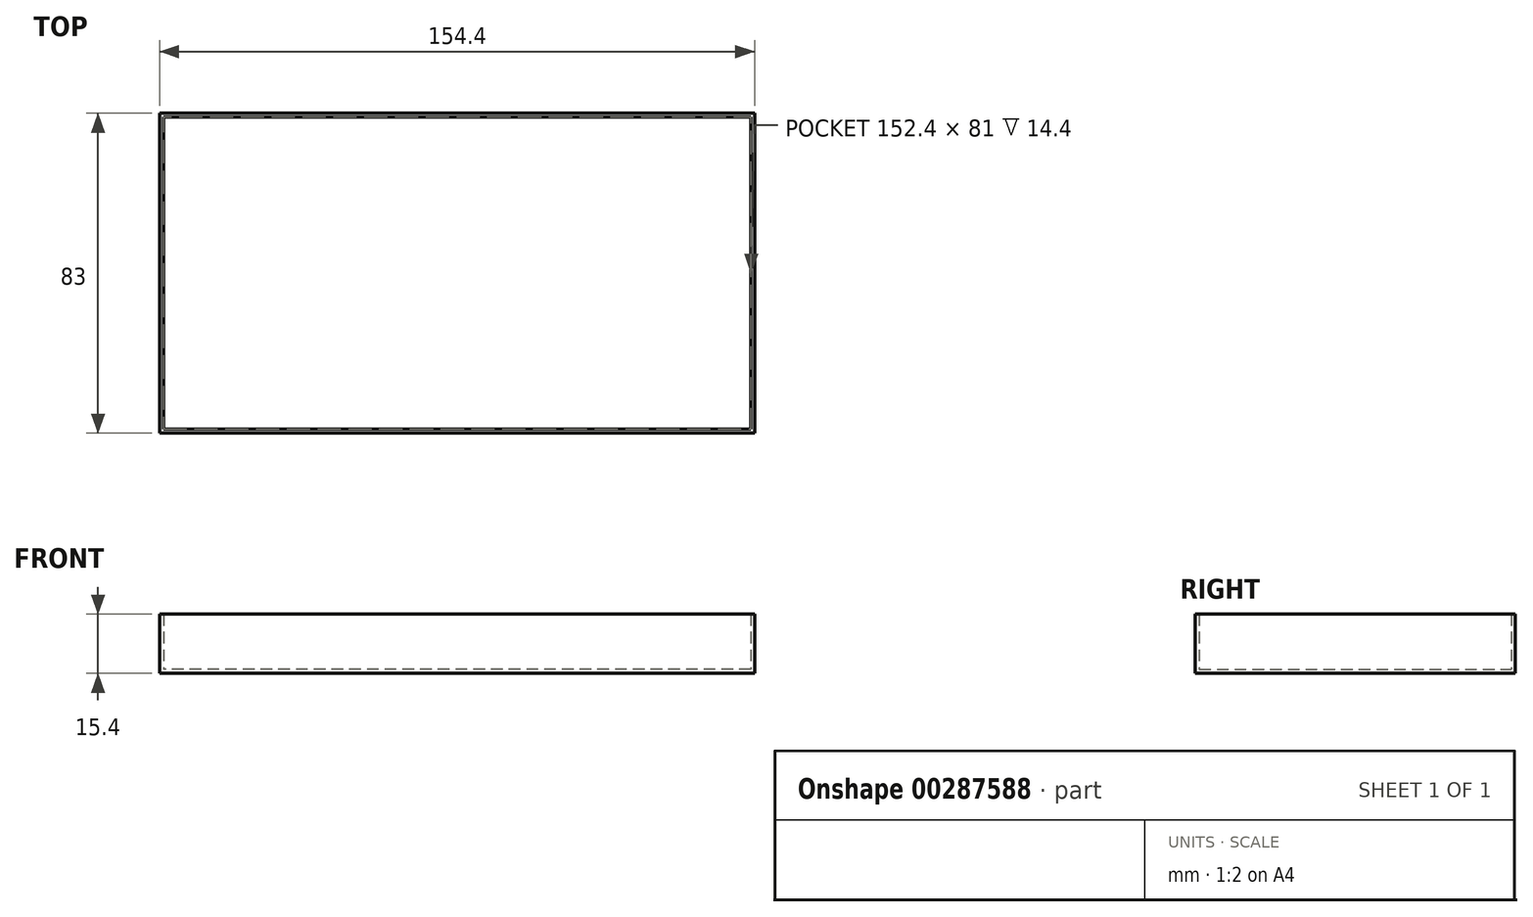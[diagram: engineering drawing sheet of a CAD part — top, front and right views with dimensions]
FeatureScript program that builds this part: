
annotation { "Feature Type Name" : "Feature", "Feature Type Description" : "" }
export const myFeature = defineFeature(function(context is Context, id is Id, definition is map)
    precondition{}
    {
        {
            var Q0;
            Q0=qCreatedBy(makeId("Top.planeOp"),FACE);
            var sketch = newSketch(context, id + "F0", { "sketchPlane" : qUnion([Q0])});
            skLineSegment(sketch, "E0.bottom", {"start": v(76.2, -40.5) * mm, "end": v(-76.2, -40.5) * mm});
            skLineSegment(sketch, "E0.top", {"start": v(76.2, 40.5) * mm, "end": v(-76.2, 40.5) * mm});
            skLineSegment(sketch, "E0.left", {"start": v(76.2, -40.5) * mm, "end": v(76.2, 40.5) * mm});
            skLineSegment(sketch, "E0.right", {"start": v(-76.2, -40.5) * mm, "end": v(-76.2, 40.5) * mm});
            skPoint(sketch, "E0.middle", {"position": v(0, 0) * mm});
            skLineSegment(sketch, "E1.bottom", {"start": v(77.2, -41.5) * mm, "end": v(-77.2, -41.5) * mm});
            skLineSegment(sketch, "E1.top", {"start": v(77.2, 41.5) * mm, "end": v(-77.2, 41.5) * mm});
            skLineSegment(sketch, "E1.left", {"start": v(77.2, -41.5) * mm, "end": v(77.2, 41.5) * mm});
            skLineSegment(sketch, "E1.right", {"start": v(-77.2, -41.5) * mm, "end": v(-77.2, 41.5) * mm});
            skSolve(sketch);
        }
        {
            var Q0;
            Q0=makeQuery(id+"F0.imprint","IMPRINT",FACE,{"disambiguationData":[TD([[makeQuery(id+"F0.imprint","IMPRINT",EDGE,{"derivedFrom":sQuery(id+"F0.wireOp",EDGE,"E0.bottom")}),-1.0]])]});
            extrude(context, id + "F1", {"entities" : qUnion([Q0]), "depth" : 1 * mm, "offsetDistance" : 25 * mm});
        }
        {
            var Q0;
            Q0=makeQuery(id+"F0.imprint","IMPRINT",FACE,{"disambiguationData":[TD([[makeQuery(id+"F0.imprint","IMPRINT",EDGE,{"derivedFrom":sQuery(id+"F0.wireOp",EDGE,"E0.bottom")}),1.0]])]});
            extrude(context, id + "F2", {"entities" : qUnion([Q0]), "operationType" : NewBodyOperationType.ADD, "depth" : 15.4 * mm, "offsetDistance" : 25 * mm});
        }
    });
